# Revit family: VCB61_VCB62
name_source: partatom
category: Specialty Equipment
revit_build: Autodesk Revit MEP 2012 (Build: 20110916_2132(x64)
units: mm (PartAtom-declared; Revit-internal decimal feet)

## types (2) — shared parameters
Apparent Power = 0 VA
Assembly Code = E1090320
Conn Conduit = Yes
Cycle = 50 Hz
Depth = 350 mm
Description = VERTICAL CUTTER BLENDER 6 LITER
Elec Conn Connection Height = 50 mm  [stored 0.164042 ft]
FL Amps = 0 A
Height = 480 mm
Manufacturer = HALLDE
Max Overcurrent Protection = 10 A
Min Ckt Ampacity = 0 A
Phase = 1
URL = www.hallde.com
Volts = 230 V
Width = 310 mm

## per-type parameters (varying)
| type | Watts | Weight |
| VCB-61 | 900 W | 27,5 kg |
| VCB-62 | 1500 W | 24 kg |

note: column(s) folded — value = type name in every type: Model

note: [stored X ft] marks values corroborated as IEEE doubles in the binary element streams (Revit-internal decimal feet)

## geometry (parser evidence)
native form markers: Blend x12, Sweep x2
no freeform markers — native parametric forms only
